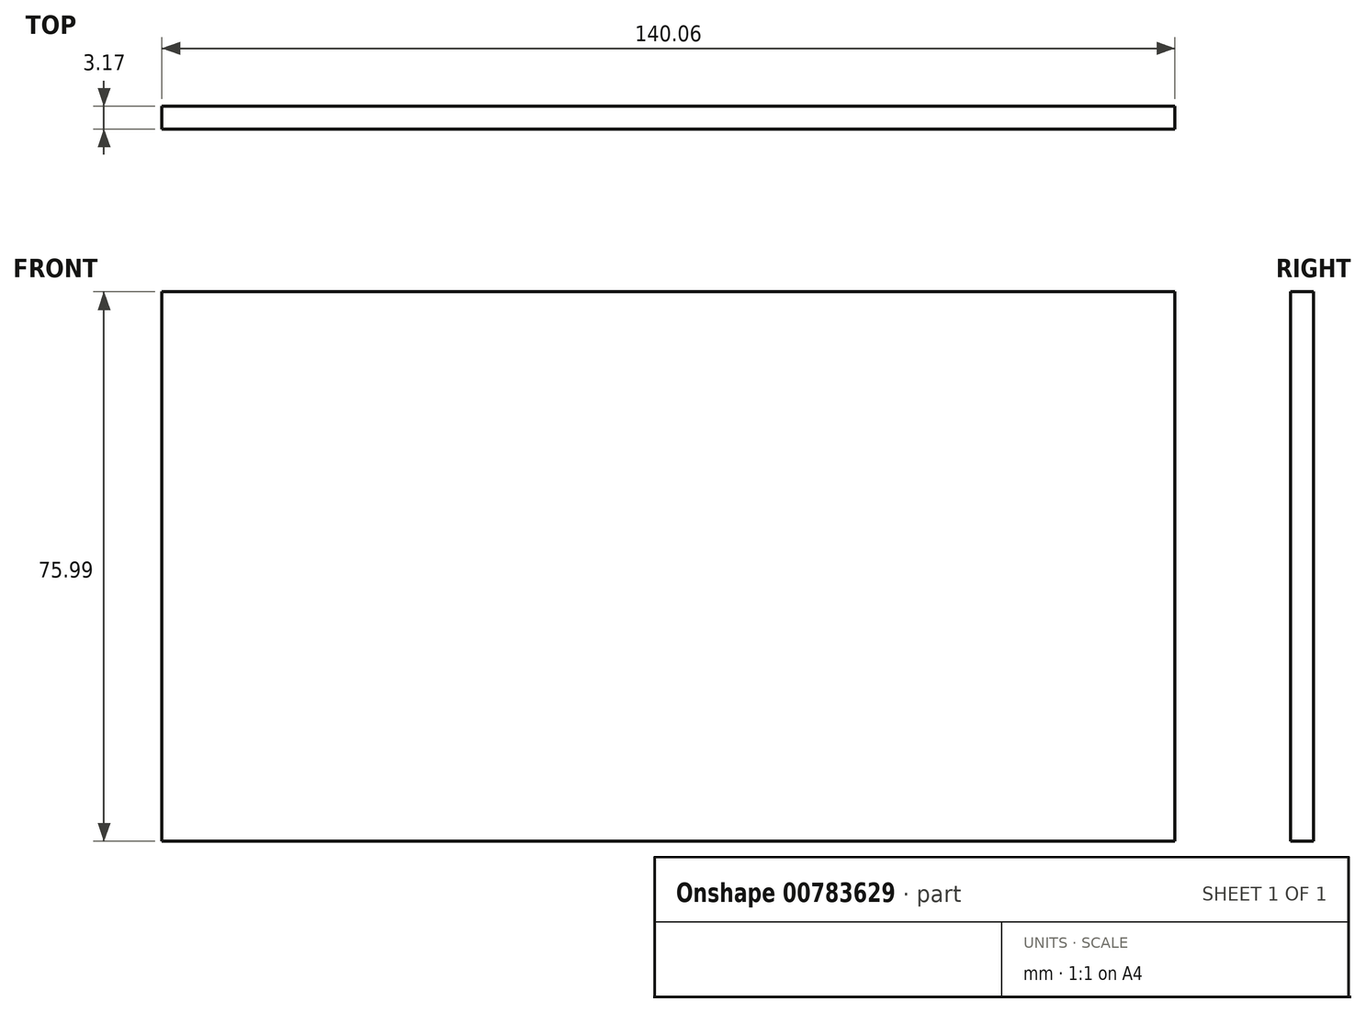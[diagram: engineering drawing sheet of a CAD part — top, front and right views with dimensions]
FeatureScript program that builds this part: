
annotation { "Feature Type Name" : "Feature", "Feature Type Description" : "" }
export const myFeature = defineFeature(function(context is Context, id is Id, definition is map)
    precondition{}
    {
        {
            var Q0;
            Q0=qCreatedBy(makeId("Front.planeOp"),FACE);
            var sketch = newSketch(context, id + "F0", { "sketchPlane" : qUnion([Q0])});
            skLineSegment(sketch, "E0.bottom", {"start": v(-70.35, 37.35) * mm, "end": v(69.7, 37.35) * mm});
            skLineSegment(sketch, "E0.top", {"start": v(-70.35, -38.64) * mm, "end": v(69.7, -38.64) * mm});
            skLineSegment(sketch, "E0.left", {"start": v(-70.35, 37.35) * mm, "end": v(-70.35, -38.64) * mm});
            skLineSegment(sketch, "E0.right", {"start": v(69.7, 37.35) * mm, "end": v(69.7, -38.64) * mm});
            skSolve(sketch);
        }
        {
            var Q0;
            Q0=makeQuery(id+"F0.imprint","IMPRINT",FACE,{"disambiguationData":[TD([[makeQuery(id+"F0.imprint","IMPRINT",EDGE,{"derivedFrom":sQuery(id+"F0.wireOp",EDGE,"E0.bottom")}),-1.0]])]});
            extrude(context, id + "F1", {"entities" : qUnion([Q0]), "depth" : 3.17 * mm, "offsetDistance" : 25.4 * mm, "hasSecondDirection" : true, "secondDirectionOppositeDirection" : true, "secondDirectionDepth" : 0 * mm});
        }
    });
